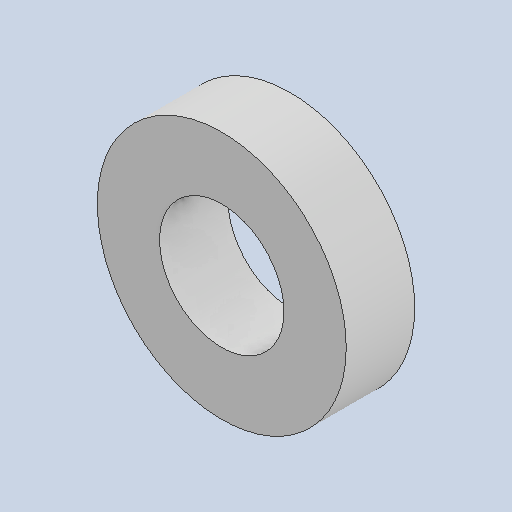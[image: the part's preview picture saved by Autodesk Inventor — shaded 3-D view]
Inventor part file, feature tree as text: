
AUTODESK INVENTOR PART (.ipt)
format: ipt  version: 2024.3 (Build 283343000, 343)  size: 217,088 bytes
history: native  units: mm
features: other x1, extrude x1, sketch x1
ambient origin geometry x8: Origin, YZ Plane, XZ Plane, XY Plane, X Axis, Y Axis, Z Axis, Center Point
bodies: Body1 (feature_tree)
feature tree (3):
  other  "ソリッド1"
  extrude  "押し出し1"  Depth=10.0mm
  sketch  "スケッチ1"
